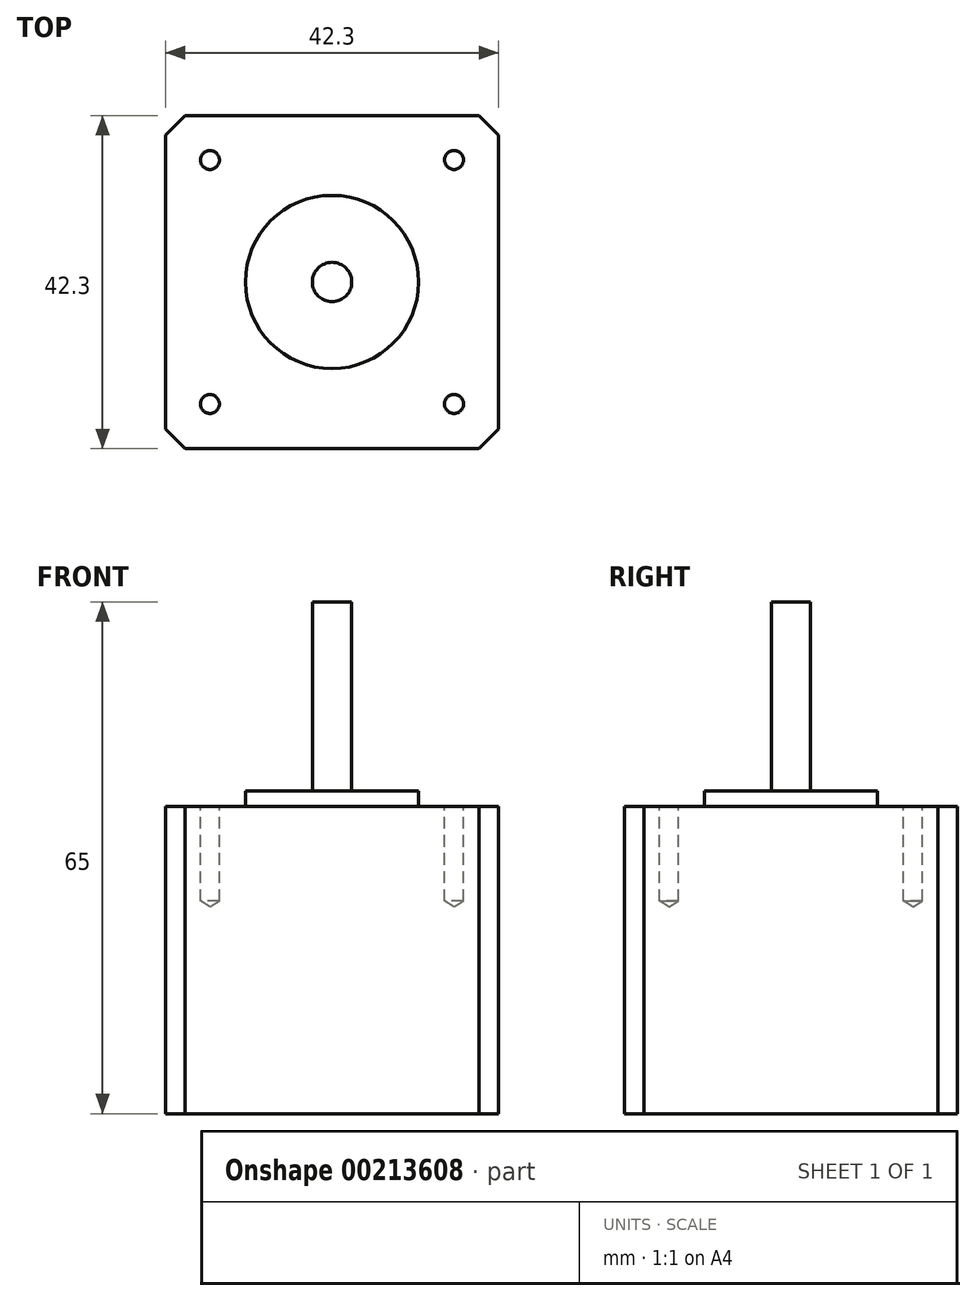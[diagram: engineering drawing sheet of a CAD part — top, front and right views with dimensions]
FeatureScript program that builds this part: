
annotation { "Feature Type Name" : "Feature", "Feature Type Description" : "" }
export const myFeature = defineFeature(function(context is Context, id is Id, definition is map)
    precondition{}
    {
        {
            var Q0;
            Q0=qCreatedBy(makeId("Top.planeOp"),FACE);
            var sketch = newSketch(context, id + "F0", { "sketchPlane" : qUnion([Q0])});
            skLineSegment(sketch, "E0.bottom", {"start": v(0, 0) * mm, "end": v(42.3, 0) * mm});
            skLineSegment(sketch, "E0.top", {"start": v(0, 42.3) * mm, "end": v(42.3, 42.3) * mm});
            skLineSegment(sketch, "E0.left", {"start": v(0, 0) * mm, "end": v(0, 42.3) * mm});
            skLineSegment(sketch, "E0.right", {"start": v(42.3, 0) * mm, "end": v(42.3, 42.3) * mm});
            skSolve(sketch);
        }
        {
            var Q0;
            Q0 = qSketchRegion(id + "F0", true);
            extrude(context, id + "F1", {"entities" : qUnion([Q0]), "depth" : 39 * mm});
        }
        {
            var Q0;
            Q0=makeQuery(id+"F1.opExtrude","CAP_FACE",FACE,{"disambiguationData":[OSD([sQuery(id+"F0.wireOp",EDGE,"E0.bottom"),sQuery(id+"F0.wireOp",EDGE,"E0.top"),sQuery(id+"F0.wireOp",EDGE,"E0.left"),sQuery(id+"F0.wireOp",EDGE,"E0.right")])],"isStart":false});
            var sketch = newSketch(context, id + "F2", { "sketchPlane" : qUnion([Q0])});
            skCircle(sketch, "E1", {"center": v(21.15, 21.15) * mm, "radius": 11 * mm});
            skSolve(sketch);
        }
        {
            var Q0;
            Q0 = qSketchRegion(id + "F2", true);
            extrude(context, id + "F3", {"entities" : qUnion([Q0]), "operationType" : NewBodyOperationType.ADD, "depth" : 2 * mm});
        }
        {
            var Q0;
            Q0=makeQuery(id+"F3.opExtrude","CAP_FACE",FACE,{"disambiguationData":[OSD([sQuery(id+"F2.wireOp",EDGE,"E1")])],"isStart":false});
            var sketch = newSketch(context, id + "F4", { "sketchPlane" : qUnion([Q0])});
            skCircle(sketch, "E2", {"center": v(21.15, 21.15) * mm, "radius": 2.5 * mm});
            skSolve(sketch);
        }
        {
            var Q0;
            Q0 = qSketchRegion(id + "F4", true);
            var Q1;
            Q1=makeQuery(id+"F1.opExtrude","SWEPT_BODY",BODY,{"disambiguationData":[OSD([sQuery(id+"F0.wireOp",EDGE,"E0.bottom"),sQuery(id+"F0.wireOp",EDGE,"E0.top"),sQuery(id+"F0.wireOp",EDGE,"E0.left"),sQuery(id+"F0.wireOp",EDGE,"E0.right")])]});
            extrude(context, id + "F5", {"entities" : qUnion([Q0]), "operationType" : NewBodyOperationType.ADD, "depth" : 24 * mm});
        }
        {
            var Q0;
            Q0=makeQuery(id+"F1.opExtrude","SWEPT_EDGE",EDGE,{"disambiguationData":[OSD([sQuery(id+"F0.wireOp",EDGE,"E0.bottom"),sQuery(id+"F0.wireOp",EDGE,"E0.right")])]});
            var Q1;
            Q1=makeQuery(id+"F1.opExtrude","SWEPT_EDGE",EDGE,{"disambiguationData":[OSD([sQuery(id+"F0.wireOp",EDGE,"E0.top"),sQuery(id+"F0.wireOp",EDGE,"E0.right")])]});
            var Q2;
            Q2=makeQuery(id+"F1.opExtrude","SWEPT_EDGE",EDGE,{"disambiguationData":[OSD([sQuery(id+"F0.wireOp",EDGE,"E0.bottom"),sQuery(id+"F0.wireOp",EDGE,"E0.left")])]});
            var Q3;
            Q3=makeQuery(id+"F1.opExtrude","SWEPT_EDGE",EDGE,{"disambiguationData":[OSD([sQuery(id+"F0.wireOp",EDGE,"E0.top"),sQuery(id+"F0.wireOp",EDGE,"E0.left")])]});
            chamfer(context, id + "F6", {"entities" : qUnion([Q0, Q1, Q2, Q3]), "width" : 2.5 * mm, "tangentPropagation" : true});
        }
        {
            var Q0;
            Q0=makeQuery(id+"F1.opExtrude","CAP_FACE",FACE,{"disambiguationData":[OSD([sQuery(id+"F0.wireOp",EDGE,"E0.bottom"),sQuery(id+"F0.wireOp",EDGE,"E0.top"),sQuery(id+"F0.wireOp",EDGE,"E0.left"),sQuery(id+"F0.wireOp",EDGE,"E0.right")])],"isStart":false});
            var sketch = newSketch(context, id + "F7", { "sketchPlane" : qUnion([Q0])});
            skPoint(sketch, "E3", {"position": v(5.65, 36.65) * mm});
            skPoint(sketch, "E4", {"position": v(36.65, 36.65) * mm});
            skPoint(sketch, "E5", {"position": v(36.65, 5.65) * mm});
            skPoint(sketch, "E6", {"position": v(5.65, 5.65) * mm});
            skSolve(sketch);
        }
        {
            var Q0;
            Q0=sQuery(id+"F7.wireOp",VERTEX,"E3");
            var Q1;
            Q1=sQuery(id+"F7.wireOp",VERTEX,"E4");
            var Q2;
            Q2=sQuery(id+"F7.wireOp",VERTEX,"E5");
            var Q3;
            Q3=sQuery(id+"F7.wireOp",VERTEX,"E6");
            var Q4;
            Q4=makeQuery(id+"F1.opExtrude","SWEPT_BODY",BODY,{"disambiguationData":[OSD([sQuery(id+"F0.wireOp",EDGE,"E0.bottom"),sQuery(id+"F0.wireOp",EDGE,"E0.top"),sQuery(id+"F0.wireOp",EDGE,"E0.left"),sQuery(id+"F0.wireOp",EDGE,"E0.right")])]});
            hole(context, id + "F8", {"style" : HoleStyle.SIMPLE, "endStyle" : HoleEndStyle.BLIND, "standardTappedOrClearance" : lookupTablePath({ "standard" : "ISO", "engagement" : "75%", "pitch" : "0.6 mm", "size" : "M3", "type" : "Tapped" }), "standardBlindInLast" : lookupTablePath({ "standard" : "ISO", "engagement" : "75%", "pitch" : "0.6 mm", "size" : "M3", "type" : "Tapped" }), "holeDiameter" : 2.4 * mm, "holeDepth" : 12 * mm, "locations" : qUnion([Q0, Q1, Q2, Q3]), "scope" : qUnion([Q4])});
        }
    });
